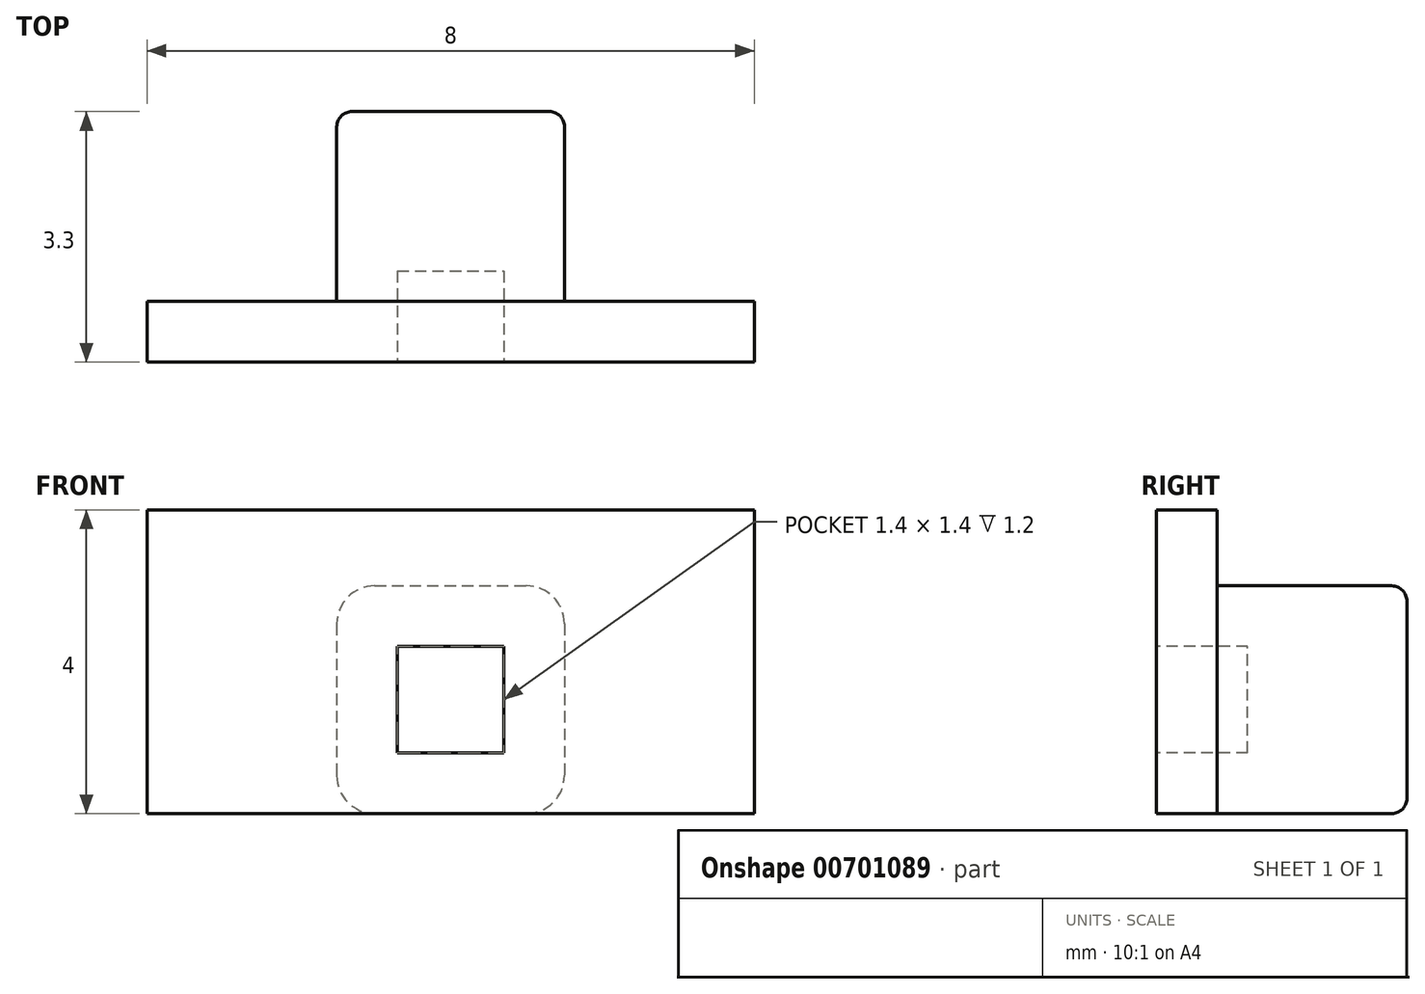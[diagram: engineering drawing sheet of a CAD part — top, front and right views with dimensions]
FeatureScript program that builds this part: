
annotation { "Feature Type Name" : "Feature", "Feature Type Description" : "" }
export const myFeature = defineFeature(function(context is Context, id is Id, definition is map)
    precondition{}
    {
        {
            var Q0;
            Q0=qCreatedBy(makeId("Top.planeOp"),FACE);
            var sketch = newSketch(context, id + "F0", { "sketchPlane" : qUnion([Q0])});
            skLineSegment(sketch, "E0.bottom", {"start": v(0, 0) * mm, "end": v(8, 0) * mm});
            skLineSegment(sketch, "E0.top", {"start": v(0, 0.8) * mm, "end": v(2.5, 0.8) * mm});
            skLineSegment(sketch, "E0.left", {"start": v(0, 0) * mm, "end": v(0, 0.8) * mm});
            skLineSegment(sketch, "E0.right", {"start": v(8, 0) * mm, "end": v(8, 0.8) * mm});
            skLineSegment(sketch, "E1", {"start": v(2.5, 0.8) * mm, "end": v(2.5, 3.3) * mm});
            skLineSegment(sketch, "E2", {"start": v(2.5, 3.3) * mm, "end": v(5.5, 3.3) * mm});
            skLineSegment(sketch, "E3", {"start": v(5.5, 3.3) * mm, "end": v(5.5, 0.8) * mm});
            skLineSegment(sketch, "E4.trimOffspring", {"start": v(5.5, 0.8) * mm, "end": v(8, 0.8) * mm});
            skSolve(sketch);
        }
        {
            var Q0;
            Q0 = qSketchRegion(id + "F0", true);
            extrude(context, id + "F1", {"entities" : qUnion([Q0]), "depth" : 3 * mm, "offsetDistance" : 25 * mm});
        }
        {
            var Q0;
            Q0=makeQuery(id+"F1.opExtrude","SWEPT_FACE",FACE,{"disambiguationData":[OSD([sQuery(id+"F0.wireOp",EDGE,"E0.bottom")])]});
            var sketch = newSketch(context, id + "F2", { "sketchPlane" : qUnion([Q0])});
            skLineSegment(sketch, "E5.bottom", {"start": v(3.3, 0.8) * mm, "end": v(4.7, 0.8) * mm});
            skLineSegment(sketch, "E5.top", {"start": v(3.3, 2.2) * mm, "end": v(4.7, 2.2) * mm});
            skLineSegment(sketch, "E5.left", {"start": v(3.3, 0.8) * mm, "end": v(3.3, 2.2) * mm});
            skLineSegment(sketch, "E5.right", {"start": v(4.7, 0.8) * mm, "end": v(4.7, 2.2) * mm});
            skLineSegment(sketch, "E6", {"start": v(0, 1.5) * mm, "end": v(1.82, 1.5) * mm, "construction": true});
            skLineSegment(sketch, "E7", {"start": v(4, 0) * mm, "end": v(4, 0.82) * mm, "construction": true});
            skSolve(sketch);
        }
        {
            var Q0;
            Q0 = qSketchRegion(id + "F2", true);
            extrude(context, id + "F3", {"entities" : qUnion([Q0]), "operationType" : NewBodyOperationType.REMOVE, "oppositeDirection" : true, "depth" : 1.2 * mm, "offsetDistance" : 25 * mm});
        }
        {
            var Q0;
            Q0=makeQuery(id+"F1.opExtrude","CAP_EDGE",EDGE,{"disambiguationData":[OSD([sQuery(id+"F0.wireOp",EDGE,"E3")])],"isStart":false});
            var Q1;
            Q1=makeQuery(id+"F1.opExtrude","CAP_EDGE",EDGE,{"disambiguationData":[OSD([sQuery(id+"F0.wireOp",EDGE,"E1")])],"isStart":false});
            var Q2;
            Q2=makeQuery(id+"F1.opExtrude","CAP_EDGE",EDGE,{"disambiguationData":[OSD([sQuery(id+"F0.wireOp",EDGE,"E1")])],"isStart":true});
            var Q3;
            Q3=makeQuery(id+"F1.opExtrude","CAP_EDGE",EDGE,{"disambiguationData":[OSD([sQuery(id+"F0.wireOp",EDGE,"E3")])],"isStart":true});
            fillet(context, id + "F4", {"entities" : qUnion([Q0, Q1, Q2, Q3]), "radius" : 0.5 * mm, "tangentPropagation" : true, "allowEdgeOverflow" : false});
        }
        {
            var Q0;
            Q0=makeQuery(id+"F1.opExtrude","CAP_EDGE",EDGE,{"disambiguationData":[OSD([sQuery(id+"F0.wireOp",EDGE,"E2")])],"isStart":false});
            var Q1;
            Q1=makeQuery(id+"F4.opFillet","BLEND_EDGE",EDGE,{"blendedFrom":[makeQuery(id+"F1.opExtrude","CAP_EDGE",EDGE,{"disambiguationData":[OSD([sQuery(id+"F0.wireOp",EDGE,"E3")])],"isStart":false}),makeQuery(id+"F1.opExtrude","SWEPT_FACE",FACE,{"disambiguationData":[OSD([sQuery(id+"F0.wireOp",EDGE,"E2")])]})],"blendedInto":[makeQuery(id+"F1.opExtrude","SWEPT_FACE",FACE,{"disambiguationData":[OSD([sQuery(id+"F0.wireOp",EDGE,"E2")])]})]});
            var Q2;
            Q2=makeQuery(id+"F1.opExtrude","SWEPT_EDGE",EDGE,{"disambiguationData":[OSD([sQuery(id+"F0.wireOp",EDGE,"E2"),sQuery(id+"F0.wireOp",EDGE,"E3")])]});
            var Q3;
            Q3=makeQuery(id+"F4.opFillet","BLEND_EDGE",EDGE,{"blendedFrom":[makeQuery(id+"F1.opExtrude","CAP_EDGE",EDGE,{"disambiguationData":[OSD([sQuery(id+"F0.wireOp",EDGE,"E3")])],"isStart":true}),makeQuery(id+"F1.opExtrude","SWEPT_FACE",FACE,{"disambiguationData":[OSD([sQuery(id+"F0.wireOp",EDGE,"E2")])]})],"blendedInto":[makeQuery(id+"F1.opExtrude","SWEPT_FACE",FACE,{"disambiguationData":[OSD([sQuery(id+"F0.wireOp",EDGE,"E2")])]})]});
            var Q4;
            Q4=makeQuery(id+"F1.opExtrude","CAP_EDGE",EDGE,{"disambiguationData":[OSD([sQuery(id+"F0.wireOp",EDGE,"E2")])],"isStart":true});
            var Q5;
            Q5=makeQuery(id+"F4.opFillet","BLEND_EDGE",EDGE,{"blendedFrom":[makeQuery(id+"F1.opExtrude","CAP_EDGE",EDGE,{"disambiguationData":[OSD([sQuery(id+"F0.wireOp",EDGE,"E1")])],"isStart":true}),makeQuery(id+"F1.opExtrude","SWEPT_FACE",FACE,{"disambiguationData":[OSD([sQuery(id+"F0.wireOp",EDGE,"E2")])]})],"blendedInto":[makeQuery(id+"F1.opExtrude","SWEPT_FACE",FACE,{"disambiguationData":[OSD([sQuery(id+"F0.wireOp",EDGE,"E2")])]})]});
            var Q6;
            Q6=makeQuery(id+"F1.opExtrude","SWEPT_EDGE",EDGE,{"disambiguationData":[OSD([sQuery(id+"F0.wireOp",EDGE,"E1"),sQuery(id+"F0.wireOp",EDGE,"E2")])]});
            var Q7;
            Q7=makeQuery(id+"F4.opFillet","BLEND_EDGE",EDGE,{"blendedFrom":[makeQuery(id+"F1.opExtrude","CAP_EDGE",EDGE,{"disambiguationData":[OSD([sQuery(id+"F0.wireOp",EDGE,"E1")])],"isStart":false}),makeQuery(id+"F1.opExtrude","SWEPT_FACE",FACE,{"disambiguationData":[OSD([sQuery(id+"F0.wireOp",EDGE,"E2")])]})],"blendedInto":[makeQuery(id+"F1.opExtrude","SWEPT_FACE",FACE,{"disambiguationData":[OSD([sQuery(id+"F0.wireOp",EDGE,"E2")])]})]});
            fillet(context, id + "F5", {"entities" : qUnion([Q0, Q1, Q2, Q3, Q4, Q5, Q6, Q7]), "radius" : 0.2 * mm, "tangentPropagation" : true, "allowEdgeOverflow" : false});
        }
        {
            var Q0;
            Q0=makeQuery(id+"F1.opExtrude","SWEPT_FACE",FACE,{"disambiguationData":[OSD([sQuery(id+"F0.wireOp",EDGE,"E0.right")])]});
            var sketch = newSketch(context, id + "F6", { "sketchPlane" : qUnion([Q0])});
            skLineSegment(sketch, "E8.bottom", {"start": v(0, 4) * mm, "end": v(0.8, 4) * mm});
            skLineSegment(sketch, "E8.left", {"start": v(0, 4) * mm, "end": v(0, 3) * mm});
            skLineSegment(sketch, "E8.right", {"start": v(0.8, 4) * mm, "end": v(0.8, 3) * mm});
            skLineSegment(sketch, "E9.0", {"start": v(0, 3) * mm, "end": v(0.8, 3) * mm});
            skSolve(sketch);
        }
        {
            var Q0;
            Q0 = qSketchRegion(id + "F6", true);
            var Q1;
            Q1=makeQuery(id+"F1.opExtrude","SWEPT_FACE",FACE,{"disambiguationData":[OSD([sQuery(id+"F0.wireOp",EDGE,"E0.left")])]});
            extrude(context, id + "F7", {"entities" : qUnion([Q0]), "operationType" : NewBodyOperationType.ADD, "endBound" : BoundingType.UP_TO_SURFACE, "oppositeDirection" : true, "depth" : 25 * mm, "endBoundEntityFace" : qUnion([Q1]), "offsetDistance" : 25 * mm});
        }
    });
